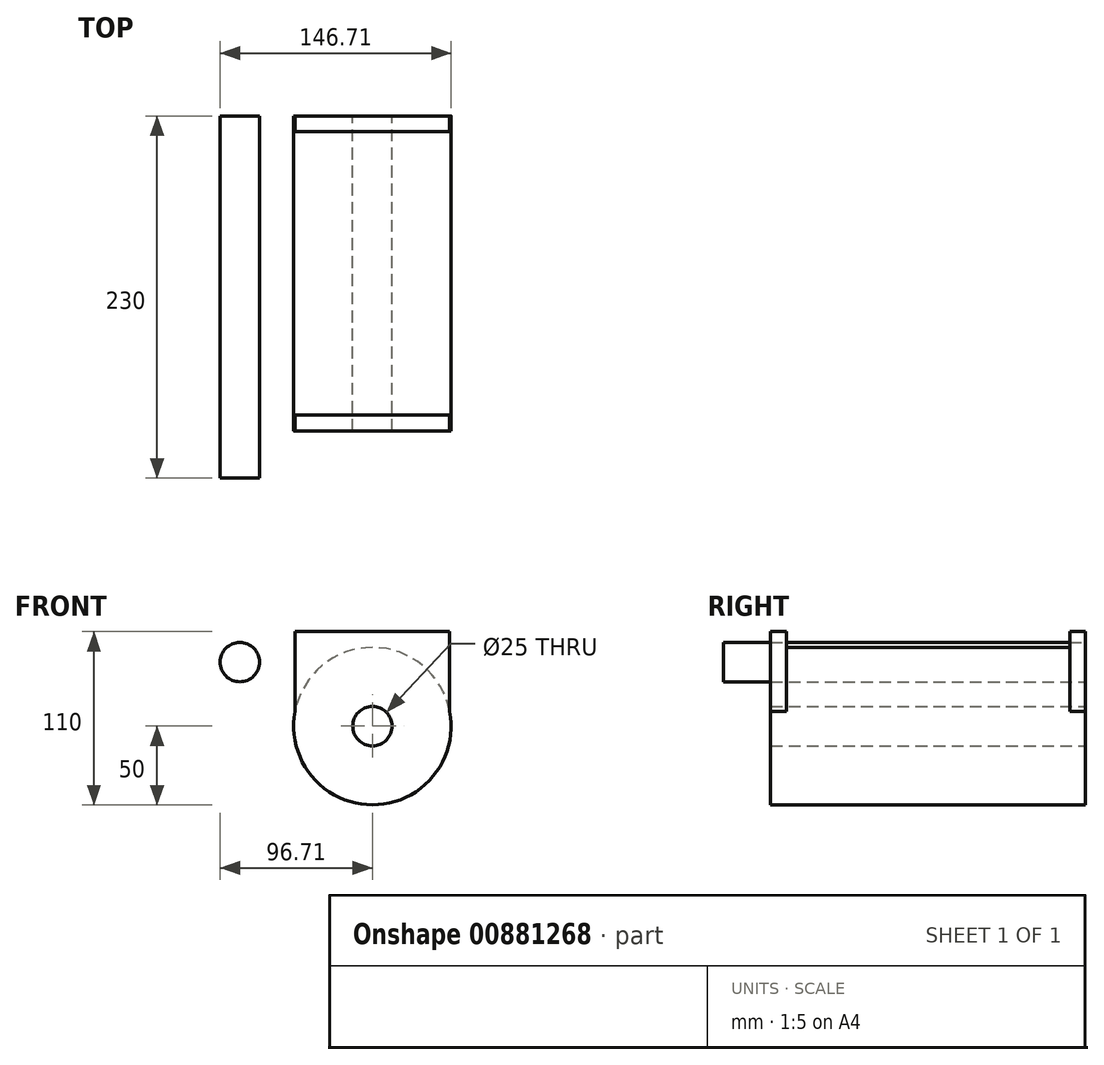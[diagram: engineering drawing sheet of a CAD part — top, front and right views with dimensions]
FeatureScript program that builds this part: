
annotation { "Feature Type Name" : "Feature", "Feature Type Description" : "" }
export const myFeature = defineFeature(function(context is Context, id is Id, definition is map)
    precondition{}
    {
        {
            var Q0;
            Q0=qCreatedBy(makeId("Front.planeOp"),FACE);
            var sketch = newSketch(context, id + "F0", { "sketchPlane" : qUnion([Q0])});
            skCircle(sketch, "E0", {"center": v(0, 0) * mm, "radius": 50 * mm});
            skCircle(sketch, "E1", {"center": v(0, 0) * mm, "radius": 12.5 * mm});
            skCircle(sketch, "E2", {"center": v(-84.21, 40.68) * mm, "radius": 12.5 * mm});
            skSolve(sketch);
        }
        {
            var Q0;
            Q0=makeQuery(id+"F0.imprint","IMPRINT",FACE,{"disambiguationData":[TD([[makeQuery(id+"F0.imprint","IMPRINT",EDGE,{"derivedFrom":sQuery(id+"F0.wireOp",EDGE,"E2")}),1.0]])]});
            extrude(context, id + "F1", {"entities" : qUnion([Q0]), "depth" : 230 * mm, "offsetDistance" : 25 * mm});
        }
        {
            var Q0;
            Q0=makeQuery(id+"F0.imprint","IMPRINT",FACE,{"disambiguationData":[TD([[makeQuery(id+"F0.imprint","IMPRINT",EDGE,{"derivedFrom":sQuery(id+"F0.wireOp",EDGE,"E0")}),1.0]])]});
            extrude(context, id + "F2", {"entities" : qUnion([Q0]), "depth" : 200 * mm, "offsetDistance" : 25 * mm});
        }
        {
            var Q0;
            Q0=qCreatedBy(makeId("Top.planeOp"),FACE);
            cPlane(context, id + "F3", {"entities" : qUnion([Q0]), "cplaneType" : CPlaneType.OFFSET, "offset" : 60 * mm, "width" : 150 * mm, "height" : 150 * mm});
        }
        {
            var Q0;
            Q0=qCreatedBy(id+"F3.planeOp",FACE);
            var sketch = newSketch(context, id + "F4", { "sketchPlane" : qUnion([Q0])});
            skLineSegment(sketch, "E3", {"start": v(0, 0) * mm, "end": v(0, -200) * mm});
            skLineSegment(sketch, "E4", {"start": v(0, -100) * mm, "end": v(46.8, -100) * mm});
            skLineSegment(sketch, "E5", {"start": v(0, -10) * mm, "end": v(49.12, -10) * mm});
            skLineSegment(sketch, "E6", {"start": v(49.12, -10) * mm, "end": v(49.12, 0) * mm});
            skLineSegment(sketch, "E7", {"start": v(49.12, 0) * mm, "end": v(0, 0) * mm});
            skLineSegment(sketch, "E8", {"start": v(0, -10) * mm, "end": v(0, 0) * mm});
            skLineSegment(sketch, "E9.MirrorCS", {"start": v(0, -10) * mm, "end": v(-49.12, -10) * mm});
            skLineSegment(sketch, "E10.MirrorCS", {"start": v(-49.12, 0) * mm, "end": v(0, 0) * mm});
            skLineSegment(sketch, "E11.MirrorCS", {"start": v(-49.12, -10) * mm, "end": v(-49.12, 0) * mm});
            skLineSegment(sketch, "E12.MirrorCS", {"start": v(49.12, -200) * mm, "end": v(0, -200) * mm});
            skLineSegment(sketch, "E13.MirrorCS", {"start": v(49.12, -190) * mm, "end": v(49.12, -200) * mm});
            skLineSegment(sketch, "E14.MirrorCS", {"start": v(0, -190) * mm, "end": v(49.12, -190) * mm});
            skLineSegment(sketch, "E15.MirrorCS", {"start": v(-49.12, -200) * mm, "end": v(0, -200) * mm});
            skLineSegment(sketch, "E16.MirrorCS", {"start": v(0, -190) * mm, "end": v(-49.12, -190) * mm});
            skLineSegment(sketch, "E17.MirrorCS", {"start": v(-49.12, -190) * mm, "end": v(-49.12, -200) * mm});
            skSolve(sketch);
        }
        {
            var Q0;
            Q0 = qSketchRegion(id + "F4", true);
            extrude(context, id + "F5", {"entities" : qUnion([Q0]), "operationType" : NewBodyOperationType.ADD, "oppositeDirection" : true, "depth" : 55 * mm, "offsetDistance" : 25 * mm});
        }
        {
            var Q0;
            Q0=makeQuery(id+"F0.imprint","IMPRINT",FACE,{"disambiguationData":[TD([[makeQuery(id+"F0.imprint","IMPRINT",EDGE,{"derivedFrom":sQuery(id+"F0.wireOp",EDGE,"E1")}),1.0]])]});
            extrude(context, id + "F6", {"entities" : qUnion([Q0]), "operationType" : NewBodyOperationType.REMOVE, "depth" : 264 * mm, "offsetDistance" : 25 * mm});
        }
    });
